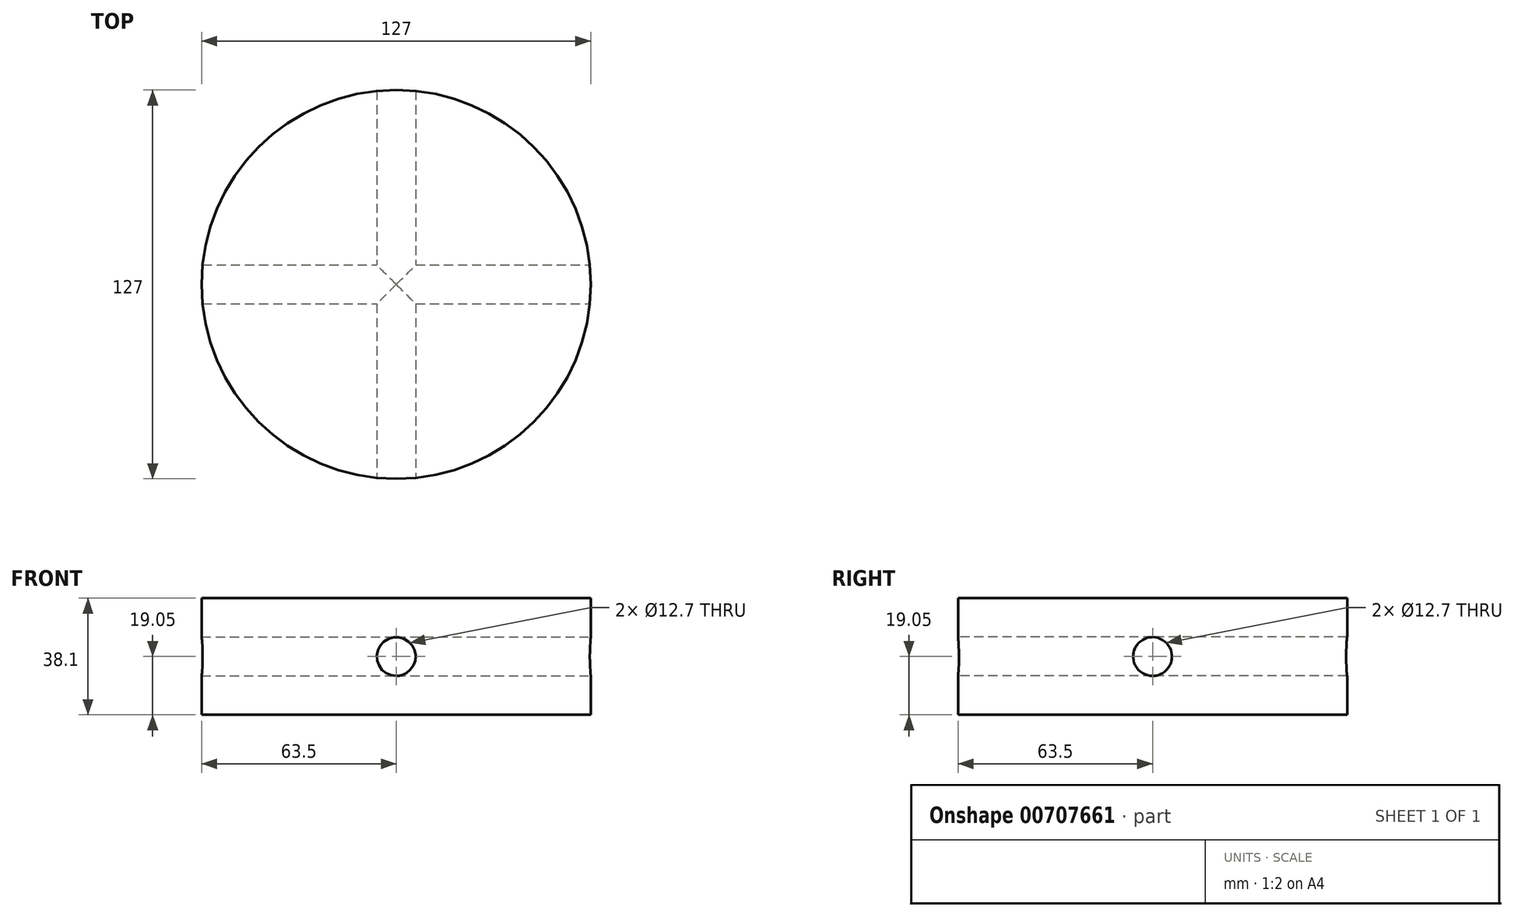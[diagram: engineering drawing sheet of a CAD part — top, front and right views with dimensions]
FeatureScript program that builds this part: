
annotation { "Feature Type Name" : "Feature", "Feature Type Description" : "" }
export const myFeature = defineFeature(function(context is Context, id is Id, definition is map)
    precondition{}
    {
        {
            var Q0;
            Q0=qCreatedBy(makeId("Top.planeOp"),FACE);
            var sketch = newSketch(context, id + "F0", { "sketchPlane" : qUnion([Q0])});
            skCircle(sketch, "E0", {"center": v(0, 0) * mm, "radius": 63.5 * mm});
            skSolve(sketch);
        }
        {
            var Q0;
            Q0 = qSketchRegion(id + "F0", true);
            extrude(context, id + "F1", {"entities" : qUnion([Q0]), "endBound" : BoundingType.SYMMETRIC, "depth" : 38.1 * mm, "offsetDistance" : 25.4 * mm});
        }
        {
            var Q0;
            Q0=qCreatedBy(makeId("Front.planeOp"),FACE);
            var sketch = newSketch(context, id + "F2", { "sketchPlane" : qUnion([Q0])});
            skCircle(sketch, "E1", {"center": v(0, 0) * mm, "radius": 6.35 * mm});
            skSolve(sketch);
        }
        {
            var Q0;
            Q0 = qSketchRegion(id + "F2", true);
            extrude(context, id + "F3", {"entities" : qUnion([Q0]), "operationType" : NewBodyOperationType.REMOVE, "endBound" : BoundingType.SYMMETRIC, "oppositeDirection" : true, "depth" : 762 * mm, "offsetDistance" : 25.4 * mm});
        }
        {
            var Q0;
            Q0=qCreatedBy(makeId("Right.planeOp"),FACE);
            var sketch = newSketch(context, id + "F4", { "sketchPlane" : qUnion([Q0])});
            skCircle(sketch, "E2", {"center": v(0, 0) * mm, "radius": 6.35 * mm});
            skSolve(sketch);
        }
        {
            var Q0;
            Q0 = qSketchRegion(id + "F4", true);
            extrude(context, id + "F5", {"entities" : qUnion([Q0]), "operationType" : NewBodyOperationType.REMOVE, "endBound" : BoundingType.SYMMETRIC, "oppositeDirection" : true, "depth" : 762 * mm, "offsetDistance" : 25.4 * mm});
        }
    });
